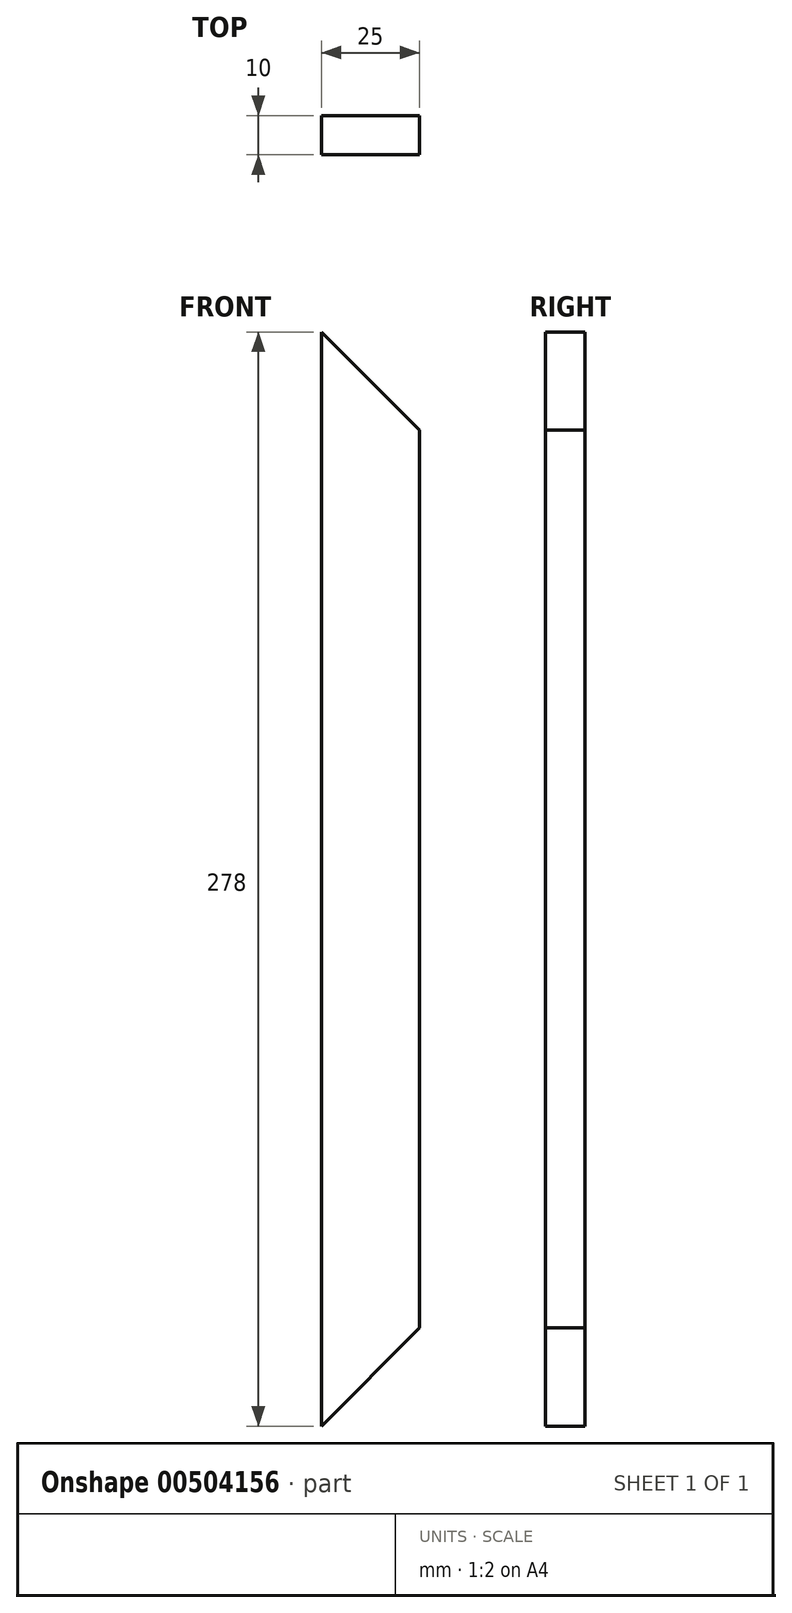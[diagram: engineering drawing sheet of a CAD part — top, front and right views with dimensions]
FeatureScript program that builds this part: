
annotation { "Feature Type Name" : "Feature", "Feature Type Description" : "" }
export const myFeature = defineFeature(function(context is Context, id is Id, definition is map)
    precondition{}
    {
        {
            var Q0;
            Q0=qCreatedBy(makeId("Front.planeOp"),FACE);
            var sketch = newSketch(context, id + "F0", { "sketchPlane" : qUnion([Q0])});
            skLineSegment(sketch, "E0.left", {"start": v(12.5, -114) * mm, "end": v(12.5, 114) * mm});
            skLineSegment(sketch, "E0.right", {"start": v(-12.5, -139) * mm, "end": v(-12.5, 139) * mm});
            skPoint(sketch, "E0.middle", {"position": v(0, 0) * mm});
            skLineSegment(sketch, "E1", {"start": v(-12.5, 139) * mm, "end": v(12.5, 114) * mm});
            skLineSegment(sketch, "E2", {"start": v(-12.5, -139) * mm, "end": v(12.5, -114) * mm});
            skLineSegment(sketch, "E3", {"start": v(0, 0) * mm, "end": v(-12.5, 0) * mm, "construction": true});
            skPoint(sketch, "E4.orphan", {"position": v(12.5, 139) * mm});
            skPoint(sketch, "E0.bottom.start.orphan", {"position": v(12.5, -139) * mm});
            skSolve(sketch);
        }
        {
            var Q0;
            Q0 = qSketchRegion(id + "F0", true);
            extrude(context, id + "F1", {"entities" : qUnion([Q0]), "depth" : 10 * mm});
        }
    });
